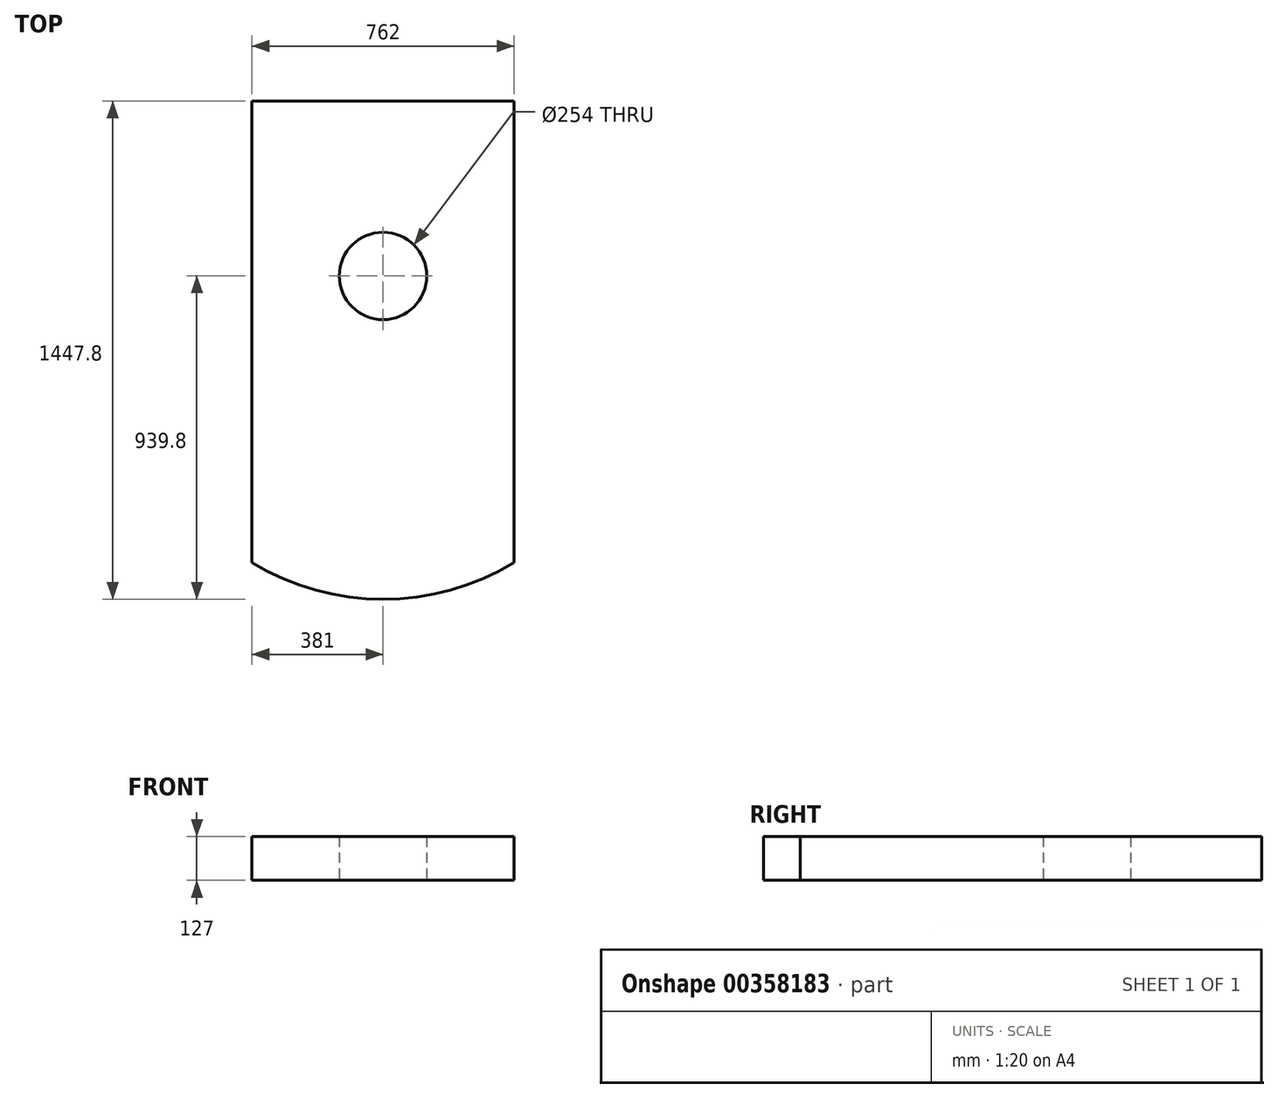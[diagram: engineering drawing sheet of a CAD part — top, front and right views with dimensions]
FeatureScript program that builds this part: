
annotation { "Feature Type Name" : "Feature", "Feature Type Description" : "" }
export const myFeature = defineFeature(function(context is Context, id is Id, definition is map)
    precondition{}
    {
        {
            var Q0;
            Q0=qCreatedBy(makeId("Top.planeOp"),FACE);
            var sketch = newSketch(context, id + "F0", { "sketchPlane" : qUnion([Q0])});
            skCircle(sketch, "E0", {"center": v(0, 0) * mm, "radius": 127 * mm});
            skLineSegment(sketch, "E1", {"start": v(0, 508) * mm, "end": v(381, 508) * mm});
            skLineSegment(sketch, "E2", {"start": v(0, 508) * mm, "end": v(-381, 508) * mm});
            skLineSegment(sketch, "E3", {"start": v(-381, 508) * mm, "end": v(-381, -833.61) * mm});
            skLineSegment(sketch, "E4", {"start": v(381, 508) * mm, "end": v(381, -833.61) * mm});
            skArc(sketch, "E5.trimOffspring", {"start": v(-381, -833.61) * mm, "mid": v(0, -939.8) * mm, "end": v(381, -833.61) * mm});
            skSolve(sketch);
        }
        {
            var Q0;
            Q0 = qSketchRegion(id + "F0", true);
            extrude(context, id + "F1", {"entities" : qUnion([Q0]), "depth" : 127 * mm});
        }
    });
